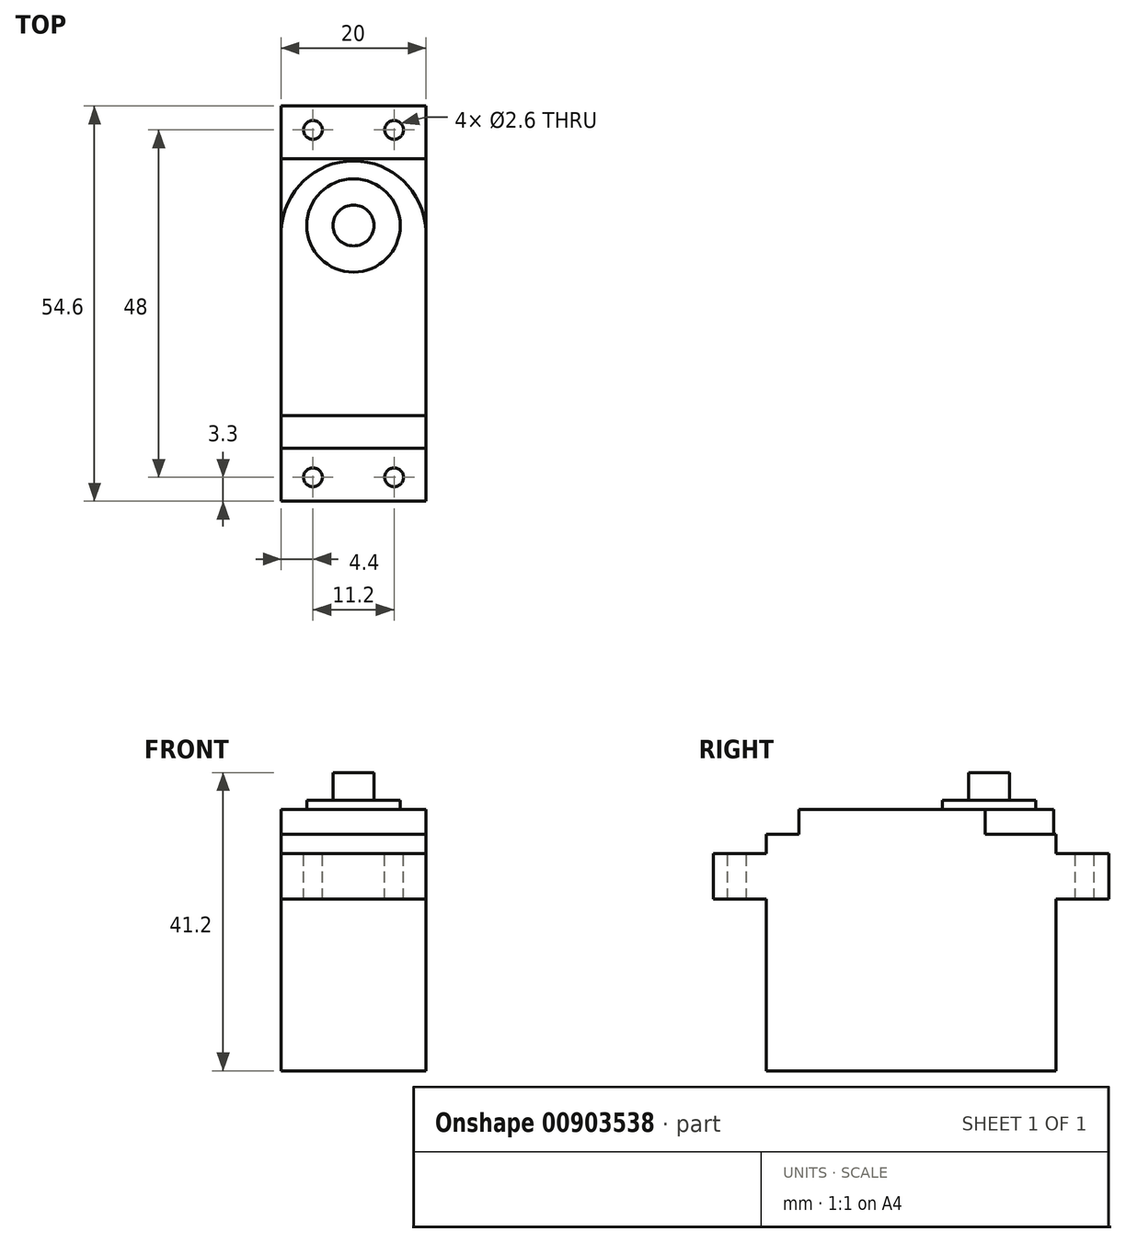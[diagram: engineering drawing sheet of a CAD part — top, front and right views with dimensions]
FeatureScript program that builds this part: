
annotation { "Feature Type Name" : "Feature", "Feature Type Description" : "" }
export const myFeature = defineFeature(function(context is Context, id is Id, definition is map)
    precondition{}
    {
        {
            var Q0;
            Q0=qCreatedBy(makeId("Top.planeOp"),FACE);
            var sketch = newSketch(context, id + "F0", { "sketchPlane" : qUnion([Q0])});
            skLineSegment(sketch, "E0.bottom", {"start": v(10, -20) * mm, "end": v(-10, -20) * mm});
            skLineSegment(sketch, "E0.top", {"start": v(10, 20) * mm, "end": v(-10, 20) * mm});
            skLineSegment(sketch, "E0.left", {"start": v(10, -20) * mm, "end": v(10, 20) * mm});
            skLineSegment(sketch, "E0.right", {"start": v(-10, -20) * mm, "end": v(-10, 20) * mm});
            skPoint(sketch, "E0.middle", {"position": v(0, 0) * mm});
            skPoint(sketch, "E1", {"position": v(0, 10.8) * mm});
            skLineSegment(sketch, "E2", {"start": v(0, 10.8) * mm, "end": v(0, 20) * mm, "construction": true});
            skCircle(sketch, "E3", {"center": v(0, 10.8) * mm, "radius": 6.45 * mm});
            skCircle(sketch, "E4", {"center": v(0, 10.8) * mm, "radius": 2.83 * mm});
            skSolve(sketch);
        }
        {
            var Q0;
            Q0=makeQuery(id+"F0.imprint","IMPRINT",FACE,{"disambiguationData":[TD([[makeQuery(id+"F0.imprint","IMPRINT",EDGE,{"derivedFrom":sQuery(id+"F0.wireOp",EDGE,"E0.bottom")}),-1.0]])]});
            var Q1;
            Q1=makeQuery(id+"F0.imprint","IMPRINT",FACE,{"disambiguationData":[TD([[makeQuery(id+"F0.imprint","IMPRINT",EDGE,{"derivedFrom":sQuery(id+"F0.wireOp",EDGE,"E3")}),1.0]])]});
            var Q2;
            Q2=makeQuery(id+"F0.imprint","IMPRINT",FACE,{"disambiguationData":[TD([[makeQuery(id+"F0.imprint","IMPRINT",EDGE,{"derivedFrom":sQuery(id+"F0.wireOp",EDGE,"E4")}),1.0]])]});
            extrude(context, id + "F1", {"entities" : qUnion([Q0, Q1, Q2]), "depth" : 36.1 * mm, "offsetDistance" : 25 * mm});
        }
        {
            var Q0;
            Q0=makeQuery(id+"F1.opExtrude","SWEPT_FACE",FACE,{"disambiguationData":[OSD([sQuery(id+"F0.wireOp",EDGE,"E0.top")])]});
            var sketch = newSketch(context, id + "F2", { "sketchPlane" : qUnion([Q0])});
            skLineSegment(sketch, "E5.bottom", {"start": v(-10, 0) * mm, "end": v(10, 0) * mm});
            skLineSegment(sketch, "E5.top", {"start": v(-10, 30) * mm, "end": v(10, 30) * mm});
            skLineSegment(sketch, "E5.left", {"start": v(-10, 0) * mm, "end": v(-10, 30) * mm});
            skLineSegment(sketch, "E5.right", {"start": v(10, 0) * mm, "end": v(10, 30) * mm});
            skLineSegment(sketch, "E6.top", {"start": v(-10, 23.7) * mm, "end": v(10, 23.7) * mm});
            skLineSegment(sketch, "E6.left", {"start": v(-10, 30) * mm, "end": v(-10, 23.7) * mm});
            skLineSegment(sketch, "E6.right", {"start": v(10, 30) * mm, "end": v(10, 23.7) * mm});
            skSolve(sketch);
        }
        {
            var Q0;
            {var subQ0=sQuery(id+"F2.wireOp",EDGE,"E5.top");Q0=makeQuery(id+"F2.imprint","IMPRINT",FACE,{"disambiguationData":[TD([[makeQuery(id+"F2.imprint","IMPRINT",EDGE,{"derivedFrom":subQ0}),-1.0]])]});}
            extrude(context, id + "F3", {"entities" : qUnion([Q0]), "operationType" : NewBodyOperationType.ADD, "depth" : 7.3 * mm, "offsetDistance" : 25 * mm});
        }
        {
            var Q0;
            Q0=makeQuery(id+"F1.opExtrude","SWEPT_FACE",FACE,{"disambiguationData":[OSD([sQuery(id+"F0.wireOp",EDGE,"E0.bottom")])]});
            var sketch = newSketch(context, id + "F4", { "sketchPlane" : qUnion([Q0])});
            skLineSegment(sketch, "E7.bottom", {"start": v(-10, 0) * mm, "end": v(10, 0) * mm});
            skLineSegment(sketch, "E7.top", {"start": v(-10, 30) * mm, "end": v(10, 30) * mm});
            skLineSegment(sketch, "E7.left", {"start": v(-10, 0) * mm, "end": v(-10, 30) * mm});
            skLineSegment(sketch, "E7.right", {"start": v(10, 0) * mm, "end": v(10, 30) * mm});
            skLineSegment(sketch, "E8.top", {"start": v(-10, 23.7) * mm, "end": v(10, 23.7) * mm});
            skLineSegment(sketch, "E8.left", {"start": v(-10, 30) * mm, "end": v(-10, 23.7) * mm});
            skLineSegment(sketch, "E8.right", {"start": v(10, 30) * mm, "end": v(10, 23.7) * mm});
            skSolve(sketch);
        }
        {
            var Q0;
            {var subQ0=sQuery(id+"F4.wireOp",EDGE,"E7.top");Q0=makeQuery(id+"F4.imprint","IMPRINT",FACE,{"disambiguationData":[TD([[makeQuery(id+"F4.imprint","IMPRINT",EDGE,{"derivedFrom":subQ0}),-1.0]])]});}
            extrude(context, id + "F5", {"entities" : qUnion([Q0]), "operationType" : NewBodyOperationType.ADD, "depth" : 7.3 * mm, "offsetDistance" : 25 * mm});
        }
        {
            var Q0;
            Q0=makeQuery(id+"F0.imprint","IMPRINT",FACE,{"disambiguationData":[TD([[makeQuery(id+"F0.imprint","IMPRINT",EDGE,{"derivedFrom":sQuery(id+"F0.wireOp",EDGE,"E4")}),1.0]])]});
            extrude(context, id + "F6", {"entities" : qUnion([Q0]), "operationType" : NewBodyOperationType.ADD, "depth" : 41.2 * mm, "offsetDistance" : 25 * mm});
        }
        {
            var Q0;
            Q0=makeQuery(id+"F0.imprint","IMPRINT",FACE,{"disambiguationData":[TD([[makeQuery(id+"F0.imprint","IMPRINT",EDGE,{"derivedFrom":sQuery(id+"F0.wireOp",EDGE,"E3")}),1.0]])]});
            extrude(context, id + "F7", {"entities" : qUnion([Q0]), "operationType" : NewBodyOperationType.ADD, "depth" : 37.4 * mm, "offsetDistance" : 25 * mm});
        }
        {
            var Q0;
            Q0=makeQuery(id+"F5.opExtrude","SWEPT_FACE",FACE,{"disambiguationData":[OSD([sQuery(id+"F4.wireOp",EDGE,"E7.top")])]});
            var sketch = newSketch(context, id + "F8", { "sketchPlane" : qUnion([Q0])});
            skPoint(sketch, "E9", {"position": v(5.6, -24) * mm});
            skLineSegment(sketch, "E10", {"start": v(5.6, -24) * mm, "end": v(5.6, -27.3) * mm, "construction": true});
            skLineSegment(sketch, "E11", {"start": v(5.6, -24) * mm, "end": v(10, -24) * mm, "construction": true});
            skCircle(sketch, "E12", {"center": v(5.6, -24) * mm, "radius": 1.3 * mm});
            skCircle(sketch, "E13.0.1.0", {"center": v(5.6, 24) * mm, "radius": 1.3 * mm});
            skCircle(sketch, "E13.1.0.0", {"center": v(-5.6, -24) * mm, "radius": 1.3 * mm});
            skCircle(sketch, "E13.1.1.0", {"center": v(-5.6, 24) * mm, "radius": 1.3 * mm});
            skLineSegment(sketch, "E13.direction1", {"start": v(5.6, -24) * mm, "end": v(-5.6, -24) * mm, "construction": true});
            skLineSegment(sketch, "E13.direction2", {"start": v(5.6, -24) * mm, "end": v(5.6, 24) * mm, "construction": true});
            skLineSegment(sketch, "E14", {"start": v(-5.6, -24) * mm, "end": v(-10, -24) * mm, "construction": true});
            skLineSegment(sketch, "E15", {"start": v(-5.6, -24) * mm, "end": v(-5.6, -27.3) * mm, "construction": true});
            skSolve(sketch);
        }
        {
            var Q0;
            Q0=makeQuery(id+"F1.opExtrude","CAP_FACE",FACE,{"disambiguationData":[OSD([sQuery(id+"F0.wireOp",EDGE,"E0.bottom"),sQuery(id+"F0.wireOp",EDGE,"E0.top"),sQuery(id+"F0.wireOp",EDGE,"E0.left"),sQuery(id+"F0.wireOp",EDGE,"E0.right")])],"isStart":false});
            var sketch = newSketch(context, id + "F9", { "sketchPlane" : qUnion([Q0])});
            skPoint(sketch, "E16", {"position": v(0, 10.8) * mm});
            skArc(sketch, "E17", {"start": v(-10, 9.19) * mm, "mid": v(-0.26, 19.7) * mm, "end": v(10.01, 9.7) * mm});
            skLineSegment(sketch, "E18.bottom", {"start": v(10, -20) * mm, "end": v(-10, -20) * mm});
            skLineSegment(sketch, "E18.top", {"start": v(10, -15.5) * mm, "end": v(-10, -15.5) * mm});
            skLineSegment(sketch, "E18.left", {"start": v(10, -20) * mm, "end": v(10, -15.5) * mm});
            skLineSegment(sketch, "E18.right", {"start": v(-10, -20) * mm, "end": v(-10, -15.5) * mm});
            skSolve(sketch);
        }
        {
            var Q0;
            {var subQ5=makeQuery(id+"F1.opExtrude","CAP_EDGE",EDGE,{"disambiguationData":[OSD([sQuery(id+"F0.wireOp",EDGE,"E0.top")])],"isStart":false});Q0=makeQuery(id+"F9.imprint","IMPRINT",FACE,{"disambiguationData":[TD([[makeQuery(id+"F9.imprint","IMPRINT",EDGE,{"derivedFrom":subQ5}),1.0]])]});}
            var Q1;
            Q1=makeQuery(id+"F9.imprint","IMPRINT",FACE,{"disambiguationData":[TD([[makeQuery(id+"F9.imprint","IMPRINT",EDGE,{"derivedFrom":sQuery(id+"F9.wireOp",EDGE,"E18.bottom")}),-1.0]])]});
            extrude(context, id + "F10", {"entities" : qUnion([Q0, Q1]), "operationType" : NewBodyOperationType.REMOVE, "oppositeDirection" : true, "depth" : 3.4 * mm, "offsetDistance" : 25 * mm});
        }
        {
            var Q0;
            Q0=makeQuery(id+"F8.imprint","IMPRINT",FACE,{"disambiguationData":[TD([[makeQuery(id+"F8.imprint","IMPRINT",EDGE,{"derivedFrom":sQuery(id+"F8.wireOp",EDGE,"E12")}),1.0]])]});
            var Q1;
            Q1=makeQuery(id+"F8.imprint","IMPRINT",FACE,{"disambiguationData":[TD([[makeQuery(id+"F8.imprint","IMPRINT",EDGE,{"derivedFrom":sQuery(id+"F8.wireOp",EDGE,"E13.1.0.0")}),1.0]])]});
            var Q2;
            Q2=makeQuery(id+"F8.imprint","IMPRINT",FACE,{"disambiguationData":[TD([[makeQuery(id+"F8.imprint","IMPRINT",EDGE,{"derivedFrom":sQuery(id+"F8.wireOp",EDGE,"E13.0.1.0")}),1.0]])]});
            var Q3;
            Q3=makeQuery(id+"F8.imprint","IMPRINT",FACE,{"disambiguationData":[TD([[makeQuery(id+"F8.imprint","IMPRINT",EDGE,{"derivedFrom":sQuery(id+"F8.wireOp",EDGE,"E13.1.1.0")}),1.0]])]});
            var Q4;
            Q4=sQuery(id+"F8.wireOp",EDGE,"E13.1.1.0");
            var Q5;
            Q5=sQuery(id+"F8.wireOp",EDGE,"E13.0.1.0");
            var Q6;
            Q6=sQuery(id+"F8.wireOp",EDGE,"E12");
            var Q7;
            Q7=sQuery(id+"F8.wireOp",EDGE,"E13.1.0.0");
            extrude(context, id + "F11", {"entities" : qUnion([Q0, Q1, Q2, Q3]), "operationType" : NewBodyOperationType.REMOVE, "surfaceEntities" : qUnion([Q4, Q5, Q6, Q7]), "oppositeDirection" : true, "depth" : 8 * mm, "offsetDistance" : 25 * mm});
        }
    });
